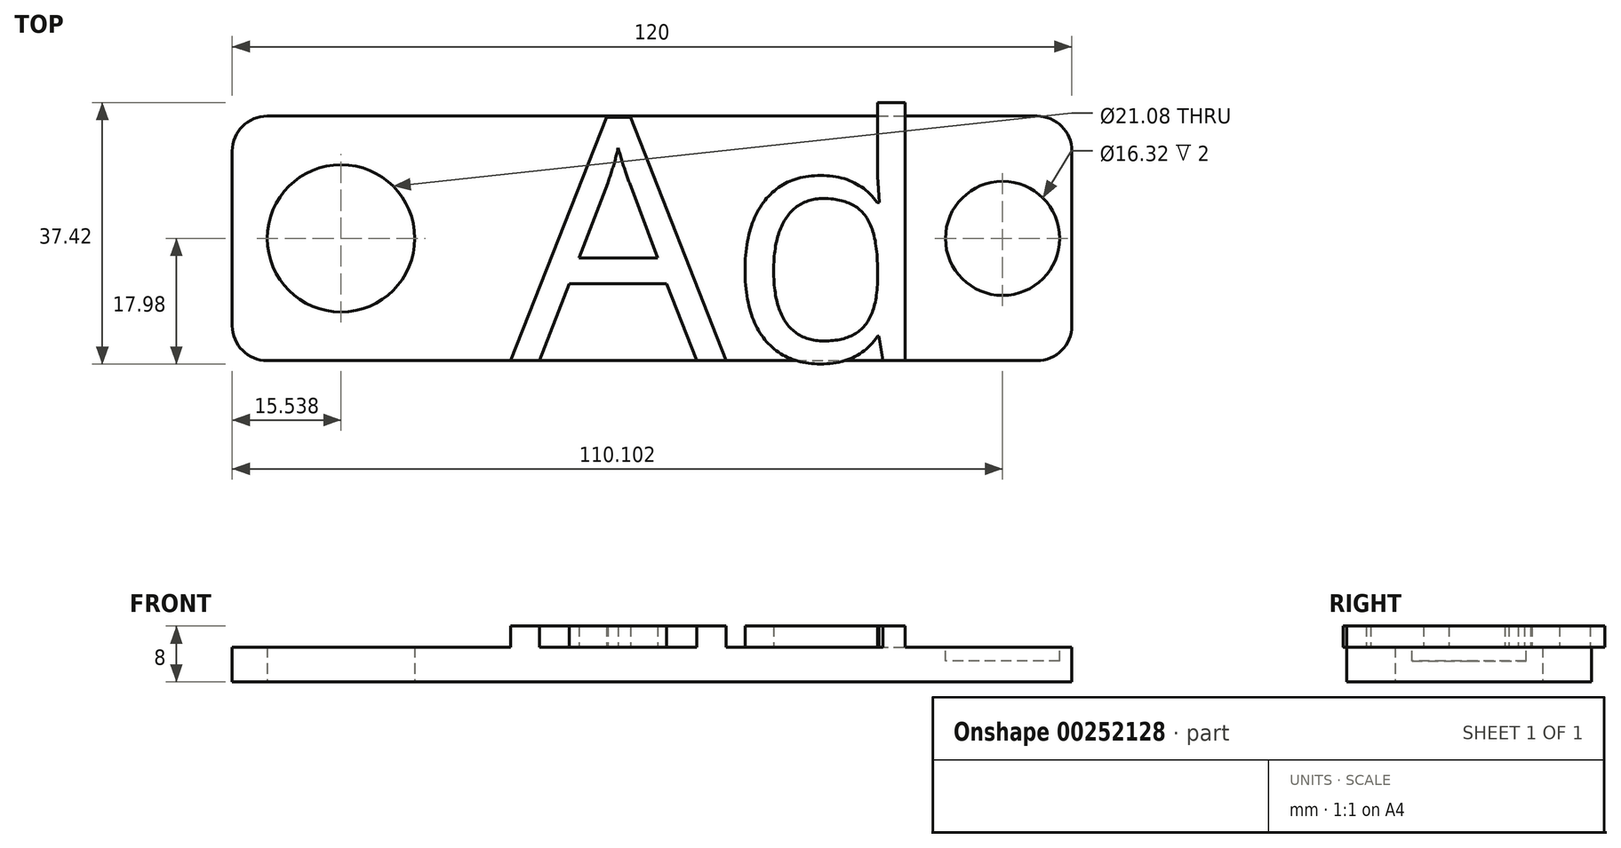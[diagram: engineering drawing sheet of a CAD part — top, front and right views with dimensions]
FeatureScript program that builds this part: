
annotation { "Feature Type Name" : "Feature", "Feature Type Description" : "" }
export const myFeature = defineFeature(function(context is Context, id is Id, definition is map)
    precondition{}
    {
        {
            var Q0;
            Q0=qCreatedBy(makeId("Top.planeOp"),FACE);
            var sketch = newSketch(context, id + "F0", { "sketchPlane" : qUnion([Q0])});
            skLineSegment(sketch, "E0.bottom", {"start": v(-60, 17.5) * mm, "end": v(60, 17.5) * mm});
            skLineSegment(sketch, "E0.top", {"start": v(-60, -17.5) * mm, "end": v(60, -17.5) * mm});
            skLineSegment(sketch, "E0.left", {"start": v(-60, 17.5) * mm, "end": v(-60, -17.5) * mm});
            skLineSegment(sketch, "E0.right", {"start": v(60, 17.5) * mm, "end": v(60, -17.5) * mm});
            skPoint(sketch, "E0.middle", {"position": v(0, 0) * mm});
            skCircle(sketch, "E1", {"center": v(-44.46, 0) * mm, "radius": 10.54 * mm});
            skSolve(sketch);
        }
        {
            var Q0;
            Q0=makeQuery(id+"F0.imprint","IMPRINT",FACE,{"disambiguationData":[TD([[makeQuery(id+"F0.imprint","IMPRINT",EDGE,{"derivedFrom":sQuery(id+"F0.wireOp",EDGE,"E0.bottom")}),-1.0]])]});
            extrude(context, id + "F1", {"entities" : qUnion([Q0]), "depth" : 5 * mm});
        }
        {
            var Q0;
            Q0=makeQuery(id+"F1.opExtrude","SWEPT_EDGE",EDGE,{"disambiguationData":[OSD([sQuery(id+"F0.wireOp",EDGE,"E0.top"),sQuery(id+"F0.wireOp",EDGE,"E0.left")])]});
            var Q1;
            Q1=makeQuery(id+"F1.opExtrude","SWEPT_EDGE",EDGE,{"disambiguationData":[OSD([sQuery(id+"F0.wireOp",EDGE,"E0.top"),sQuery(id+"F0.wireOp",EDGE,"E0.right")])]});
            var Q2;
            Q2=makeQuery(id+"F1.opExtrude","SWEPT_EDGE",EDGE,{"disambiguationData":[OSD([sQuery(id+"F0.wireOp",EDGE,"E0.bottom"),sQuery(id+"F0.wireOp",EDGE,"E0.right")])]});
            var Q3;
            Q3=makeQuery(id+"F1.opExtrude","SWEPT_EDGE",EDGE,{"disambiguationData":[OSD([sQuery(id+"F0.wireOp",EDGE,"E0.bottom"),sQuery(id+"F0.wireOp",EDGE,"E0.left")])]});
            fillet(context, id + "F2", {"entities" : qUnion([Q0, Q1, Q2, Q3]), "radius" : 5 * mm, "tangentPropagation" : true, "allowEdgeOverflow" : false});
        }
        {
            var Q0;
            Q0=makeQuery(id+"F1.opExtrude","CAP_FACE",FACE,{"disambiguationData":[OSD([sQuery(id+"F0.wireOp",EDGE,"E0.bottom"),sQuery(id+"F0.wireOp",EDGE,"E0.top"),sQuery(id+"F0.wireOp",EDGE,"E0.left"),sQuery(id+"F0.wireOp",EDGE,"E0.right"),sQuery(id+"F0.wireOp",EDGE,"E1")])],"isStart":false});
            var sketch = newSketch(context, id + "F3", { "sketchPlane" : qUnion([Q0])});
            skText(sketch, "E2", { "text": "Ad", "fontName": "OpenSans-Regular.ttf"});
            const initialGuessF3  = {"E2": [-0.0202, -0.0175, 1, 0, 0.035]};
            skSetInitialGuess(sketch, initialGuessF3);
            skSolve(sketch);
        }
        {
            var Q0;
            {var subQ0=sQuery(id+"F0.wireOp",EDGE,"E0.right");Q0=makeQuery(id+"F3.imprint","IMPRINT",FACE,{"disambiguationData":[TD([[makeQuery(id+"F3.imprint","IMPRINT",EDGE,{"derivedFrom":makeQuery(id+"F1.opExtrude","CAP_EDGE",EDGE,{"disambiguationData":[OSD([subQ0])],"isStart":false})}),-1.0]])]});}
            var sketch = newSketch(context, id + "F4", { "sketchPlane" : qUnion([Q0])});
            skCircle(sketch, "E3", {"center": v(50.1, 0) * mm, "radius": 8.16 * mm});
            skSolve(sketch);
        }
        {
            var Q0;
            Q0 = qSketchRegion(id + "F3", true);
            extrude(context, id + "F5", {"entities" : qUnion([Q0]), "operationType" : NewBodyOperationType.ADD, "depth" : 3 * mm});
        }
        {
            var Q0;
            Q0=makeQuery(id+"F4.imprint","IMPRINT",FACE,{"disambiguationData":[TD([[makeQuery(id+"F4.imprint","IMPRINT",EDGE,{"derivedFrom":sQuery(id+"F4.wireOp",EDGE,"E3")}),1.0]])]});
            extrude(context, id + "F6", {"entities" : qUnion([Q0]), "operationType" : NewBodyOperationType.REMOVE, "oppositeDirection" : true, "depth" : 2 * mm});
        }
    });
